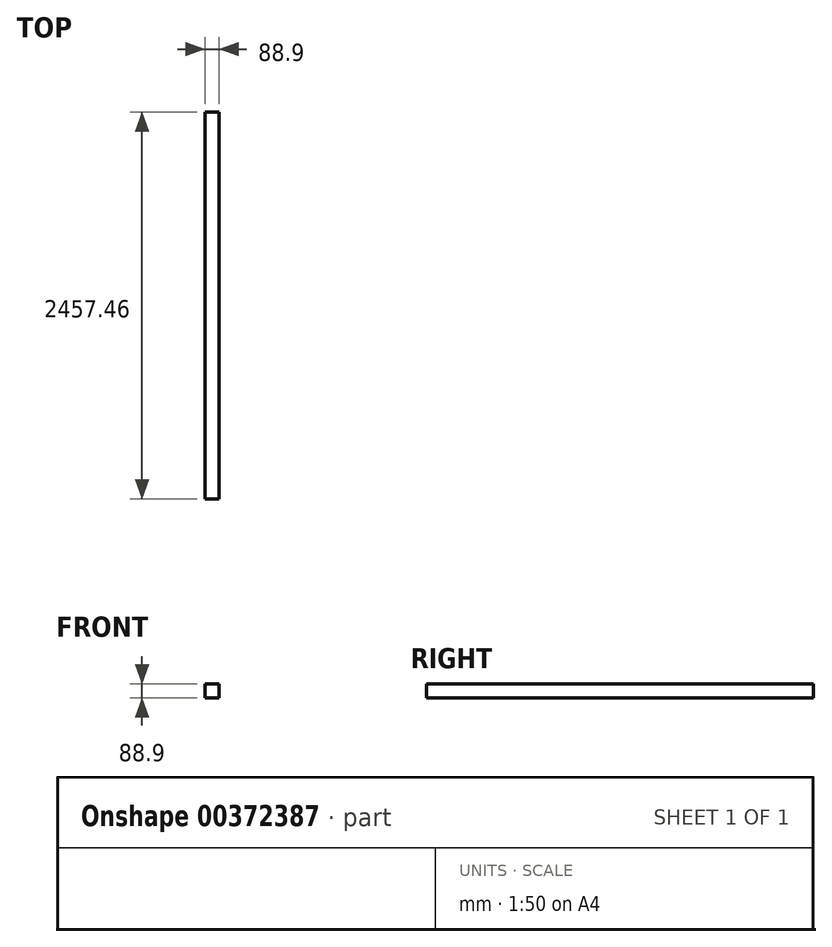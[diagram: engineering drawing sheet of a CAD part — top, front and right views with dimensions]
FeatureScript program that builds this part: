
annotation { "Feature Type Name" : "Feature", "Feature Type Description" : "" }
export const myFeature = defineFeature(function(context is Context, id is Id, definition is map)
    precondition{}
    {
        {
            var Q0;
            Q0=qCreatedBy(makeId("Front.planeOp"),FACE);
            var sketch = newSketch(context, id + "F0", { "sketchPlane" : qUnion([Q0])});
            skLineSegment(sketch, "E0.bottom", {"start": v(-44.45, 44.45) * mm, "end": v(44.45, 44.45) * mm});
            skLineSegment(sketch, "E0.top", {"start": v(-44.45, -44.45) * mm, "end": v(44.45, -44.45) * mm});
            skLineSegment(sketch, "E0.left", {"start": v(-44.45, 44.45) * mm, "end": v(-44.45, -44.45) * mm});
            skLineSegment(sketch, "E0.right", {"start": v(44.45, 44.45) * mm, "end": v(44.45, -44.45) * mm});
            skPoint(sketch, "E0.middle", {"position": v(0, 0) * mm});
            skSolve(sketch);
        }
        {
            var Q0;
            Q0=qSketchRegion(id+"F0",true);
            extrude(context, id + "F1", {"entities" : qUnion([Q0]), "endBound" : BoundingType.SYMMETRIC, "oppositeDirection" : true, "depth" : 2457.45 * mm});
        }
    });
